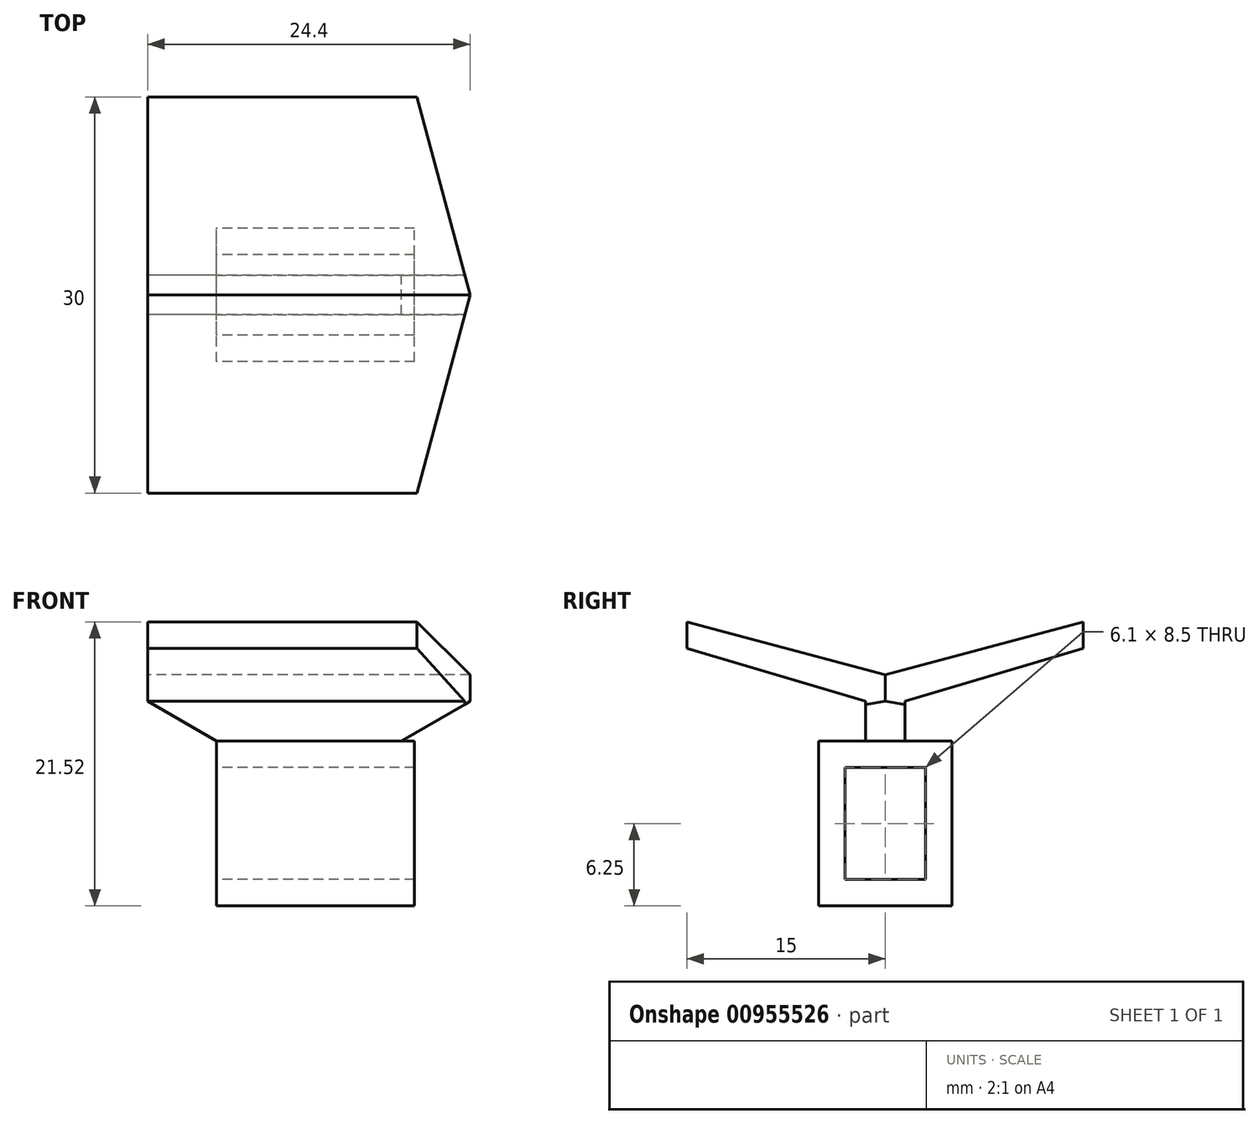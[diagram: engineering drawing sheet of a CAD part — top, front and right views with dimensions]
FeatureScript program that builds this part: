
annotation { "Feature Type Name" : "Feature", "Feature Type Description" : "" }
export const myFeature = defineFeature(function(context is Context, id is Id, definition is map)
    precondition{}
    {
        {
            var Q0;
            Q0=qCreatedBy(makeId("Right.planeOp"),FACE);
            var sketch = newSketch(context, id + "F0", { "sketchPlane" : qUnion([Q0])});
            skLineSegment(sketch, "E0.bottom", {"start": v(-3.05, 4.25) * mm, "end": v(3.05, 4.25) * mm});
            skLineSegment(sketch, "E0.top", {"start": v(-3.05, -4.25) * mm, "end": v(3.05, -4.25) * mm});
            skLineSegment(sketch, "E0.left", {"start": v(-3.05, 4.25) * mm, "end": v(-3.05, -4.25) * mm});
            skLineSegment(sketch, "E0.right", {"start": v(3.05, 4.25) * mm, "end": v(3.05, -4.25) * mm});
            skPoint(sketch, "E0.middle", {"position": v(0, 0) * mm});
            skLineSegment(sketch, "E1.bottom", {"start": v(-5.05, 6.25) * mm, "end": v(5.05, 6.25) * mm});
            skLineSegment(sketch, "E1.top", {"start": v(-5.05, -6.25) * mm, "end": v(5.05, -6.25) * mm});
            skLineSegment(sketch, "E1.left", {"start": v(-5.05, 6.25) * mm, "end": v(-5.05, -6.25) * mm});
            skLineSegment(sketch, "E1.right", {"start": v(5.05, 6.25) * mm, "end": v(5.05, -6.25) * mm});
            skSolve(sketch);
        }
        {
            var Q0;
            Q0=makeQuery(id+"F0.imprint","IMPRINT",FACE,{"disambiguationData":[TD([[makeQuery(id+"F0.imprint","IMPRINT",EDGE,{"derivedFrom":sQuery(id+"F0.wireOp",EDGE,"E0.bottom")}),1.0]])]});
            var Q1;
            Q1=qConstructionFilter(qBodyType(qCreatedBy(id+"F0",EDGE),BodyType.WIRE),ConstructionObject.NO);
            extrude(context, id + "F1", {"entities" : qUnion([Q0]), "surfaceEntities" : qUnion([Q1]), "depth" : 15 * mm, "offsetDistance" : 25 * mm});
        }
        {
            var Q0;
            Q0=qCreatedBy(makeId("Front.planeOp"),FACE);
            var sketch = newSketch(context, id + "F2", { "sketchPlane" : qUnion([Q0])});
            skLineSegment(sketch, "E2", {"start": v(0, 6.25) * mm, "end": v(14, 6.25) * mm});
            skLineSegment(sketch, "E3", {"start": v(0, 6.25) * mm, "end": v(-5.2, 9.25) * mm});
            skLineSegment(sketch, "E4", {"start": v(14, 6.25) * mm, "end": v(19.2, 9.25) * mm});
            skLineSegment(sketch, "E5", {"start": v(-5.2, 9.25) * mm, "end": v(-5.2, 11.25) * mm});
            skLineSegment(sketch, "E6", {"start": v(-5.2, 11.25) * mm, "end": v(19.2, 11.25) * mm});
            skLineSegment(sketch, "E7", {"start": v(19.2, 11.25) * mm, "end": v(19.2, 9.25) * mm});
            skSolve(sketch);
        }
        {
            var Q0;
            Q0=qSketchRegion(id+"F2",true);
            extrude(context, id + "F3", {"entities" : qUnion([Q0]), "operationType" : NewBodyOperationType.ADD, "endBound" : BoundingType.SYMMETRIC, "depth" : 3 * mm, "offsetDistance" : 25 * mm});
        }
        {
            var Q0;
            Q0=makeQuery(id+"F3.opExtrude","SWEPT_FACE",FACE,{"disambiguationData":[OSD([sQuery(id+"F2.wireOp",EDGE,"E5")])]});
            var sketch = newSketch(context, id + "F4", { "sketchPlane" : qUnion([Q0])});
            skLineSegment(sketch, "E8", {"start": v(0, 11.25) * mm, "end": v(0, 13) * mm, "construction": true});
            skPoint(sketch, "E8.endSnap0", {"position": v(0, 11.25) * mm});
            skLineSegment(sketch, "E9", {"start": v(0, 11.25) * mm, "end": v(15, 15.27) * mm});
            skLineSegment(sketch, "E10", {"start": v(0, 11.25) * mm, "end": v(10.53, 11.25) * mm, "construction": true});
            skLineSegment(sketch, "E11", {"start": v(15, 15.27) * mm, "end": v(15, 13.27) * mm});
            skLineSegment(sketch, "E12", {"start": v(15, 13.27) * mm, "end": v(1.5, 9.25) * mm});
            skLineSegment(sketch, "E13", {"start": v(1.5, 9.25) * mm, "end": v(0, 11.25) * mm});
            skLineSegment(sketch, "E14.MirrorCS", {"start": v(0, 11.25) * mm, "end": v(-15, 15.27) * mm});
            skLineSegment(sketch, "E15.MirrorCS", {"start": v(-1.5, 9.25) * mm, "end": v(0, 11.25) * mm});
            skLineSegment(sketch, "E16.MirrorCS", {"start": v(-15, 13.27) * mm, "end": v(-1.5, 9.25) * mm});
            skLineSegment(sketch, "E17.MirrorCS", {"start": v(-15, 15.27) * mm, "end": v(-15, 13.27) * mm});
            skSolve(sketch);
        }
        {
            var Q0;
            Q0=qSketchRegion(id+"F4",true);
            var Q1;
            Q1=makeQuery(id+"F3.opExtrude","SWEPT_FACE",FACE,{"disambiguationData":[OSD([sQuery(id+"F2.wireOp",EDGE,"E7")])]});
            extrude(context, id + "F5", {"entities" : qUnion([Q0]), "operationType" : NewBodyOperationType.ADD, "endBound" : BoundingType.UP_TO_SURFACE, "oppositeDirection" : true, "depth" : 25 * mm, "endBoundEntityFace" : qUnion([Q1]), "offsetDistance" : 25 * mm});
        }
        {
            var Q0;
            Q0=qCreatedBy(makeId("Top.planeOp"),FACE);
            var sketch = newSketch(context, id + "F6", { "sketchPlane" : qUnion([Q0])});
            skLineSegment(sketch, "E18", {"start": v(0, 0) * mm, "end": v(37.12, 0) * mm, "construction": true});
            skLineSegment(sketch, "E19.0", {"start": v(19.2, 0) * mm, "end": v(19.2, -15) * mm, "construction": true});
            skLineSegment(sketch, "E20", {"start": v(19.2, 0) * mm, "end": v(14.14, -18.88) * mm});
            skLineSegment(sketch, "E21", {"start": v(14.14, -18.88) * mm, "end": v(27.25, -18.88) * mm});
            skLineSegment(sketch, "E22", {"start": v(27.25, -18.88) * mm, "end": v(27.25, 0) * mm});
            skLineSegment(sketch, "E23.MirrorCS", {"start": v(19.2, 0) * mm, "end": v(14.14, 18.88) * mm});
            skLineSegment(sketch, "E24.MirrorCS", {"start": v(14.14, 18.88) * mm, "end": v(27.25, 18.88) * mm});
            skLineSegment(sketch, "E25.MirrorCS", {"start": v(27.25, 18.88) * mm, "end": v(27.25, 0) * mm});
            skSolve(sketch);
        }
        {
            var Q0;
            Q0=qSketchRegion(id+"F6",true);
            extrude(context, id + "F7", {"entities" : qUnion([Q0]), "operationType" : NewBodyOperationType.REMOVE, "depth" : 25 * mm, "offsetDistance" : 25 * mm});
        }
    });
